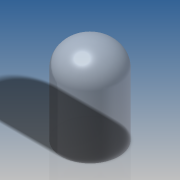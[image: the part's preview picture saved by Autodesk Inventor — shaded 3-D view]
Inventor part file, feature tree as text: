
AUTODESK INVENTOR PART (.ipt)
format: ipt  version: 2016 SP2 (Build 200236200, 236)  size: 157,696 bytes
history: native  units: in
note: dims shown in document units (in); Inventor stores cm internally (conversion verified against a paired STEP export)
features: revolve x1, sketch x1
ambient origin geometry x8: Origin, YZ Plane, XZ Plane, XY Plane, X Axis, Y Axis, Z Axis, Center Point
bodies: Solid1 (feature_tree)
feature tree (2):
  revolve  "Revolution1"  [1 undecoded]
  sketch  "Sketch2"  dims[d0=0.189in d1=0.2047in d2=0.0787in d3=90.0deg]
note: 1 required parameter value undecoded (feature->parameter linkage not recoverable at this tier; creation-order binding heuristic only, values carry confidence <= 0.55)
